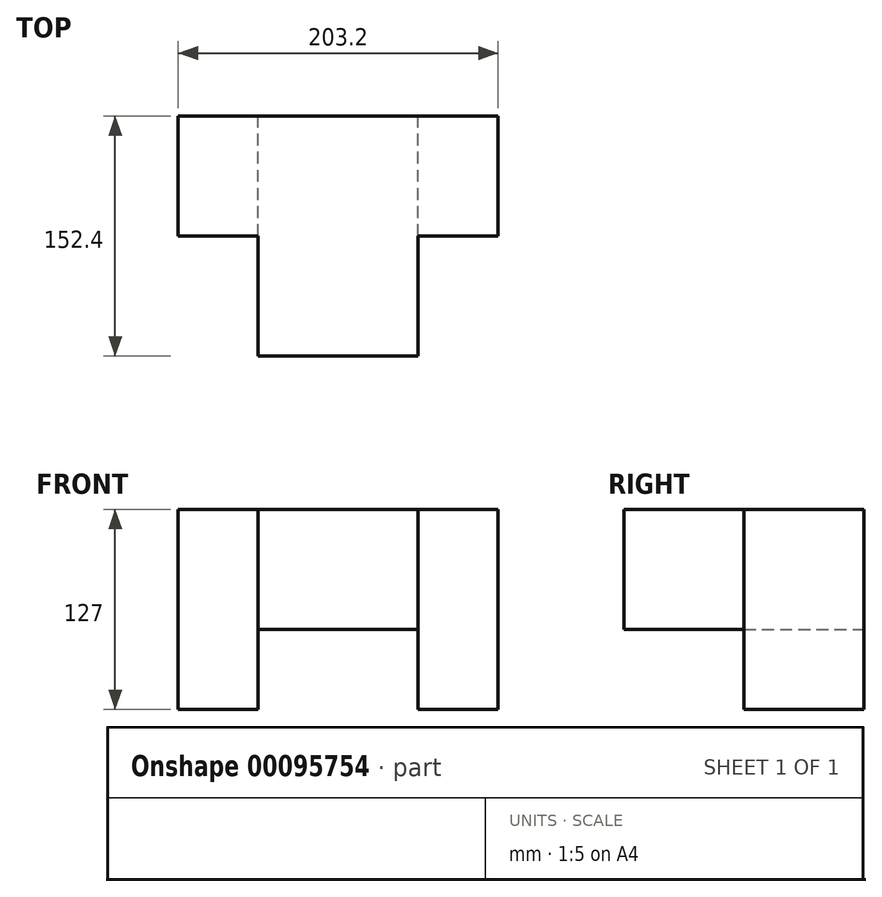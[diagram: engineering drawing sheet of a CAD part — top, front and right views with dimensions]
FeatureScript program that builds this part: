
annotation { "Feature Type Name" : "Feature", "Feature Type Description" : "" }
export const myFeature = defineFeature(function(context is Context, id is Id, definition is map)
    precondition{}
    {
        {
            var Q0;
            Q0=qCreatedBy(makeId("Front.planeOp"),FACE);
            var sketch = newSketch(context, id + "F0", { "sketchPlane" : qUnion([Q0])});
            skLineSegment(sketch, "E0.bottom", {"start": v(-54.53, 56.93) * mm, "end": v(47.07, 56.93) * mm});
            skLineSegment(sketch, "E0.top", {"start": v(-54.53, -19.27) * mm, "end": v(47.07, -19.27) * mm});
            skLineSegment(sketch, "E0.left", {"start": v(-54.53, 56.93) * mm, "end": v(-54.53, -19.27) * mm});
            skLineSegment(sketch, "E0.right", {"start": v(47.07, 56.93) * mm, "end": v(47.07, -19.27) * mm});
            skLineSegment(sketch, "E1.bottom", {"start": v(-54.53, 56.93) * mm, "end": v(-105.33, 56.93) * mm});
            skLineSegment(sketch, "E1.top", {"start": v(-54.53, -70.07) * mm, "end": v(-105.33, -70.07) * mm});
            skLineSegment(sketch, "E1.left", {"start": v(-54.53, 56.93) * mm, "end": v(-54.53, -70.07) * mm});
            skLineSegment(sketch, "E1.right", {"start": v(-105.33, 56.93) * mm, "end": v(-105.33, -70.07) * mm});
            skLineSegment(sketch, "E2.bottom", {"start": v(47.07, 56.93) * mm, "end": v(97.87, 56.93) * mm});
            skLineSegment(sketch, "E2.top", {"start": v(47.07, -70.07) * mm, "end": v(97.87, -70.07) * mm});
            skLineSegment(sketch, "E2.left", {"start": v(47.07, 56.93) * mm, "end": v(47.07, -70.07) * mm});
            skLineSegment(sketch, "E2.right", {"start": v(97.87, 56.93) * mm, "end": v(97.87, -70.07) * mm});
            skSolve(sketch);
        }
        {
            var Q0;
            Q0 = qSketchRegion(id + "F0", true);
            extrude(context, id + "F1", {"entities" : qUnion([Q0]), "depth" : 76.2 * mm});
        }
        {
            var Q0;
            Q0=makeQuery(id+"F1.opExtrude","CAP_FACE",FACE,{"disambiguationData":[OSD([sQuery(id+"F0.wireOp",EDGE,"E0.bottom"),sQuery(id+"F0.wireOp",EDGE,"E0.top"),sQuery(id+"F0.wireOp",EDGE,"E1.bottom"),sQuery(id+"F0.wireOp",EDGE,"E1.top"),sQuery(id+"F0.wireOp",EDGE,"E1.left"),sQuery(id+"F0.wireOp",EDGE,"E1.right"),sQuery(id+"F0.wireOp",EDGE,"E2.bottom"),sQuery(id+"F0.wireOp",EDGE,"E2.top"),sQuery(id+"F0.wireOp",EDGE,"E2.left"),sQuery(id+"F0.wireOp",EDGE,"E2.right")])],"isStart":false});
            var sketch = newSketch(context, id + "F2", { "sketchPlane" : qUnion([Q0])});
            skLineSegment(sketch, "E3", {"start": v(-54.53, -19.27) * mm, "end": v(-54.53, 56.93) * mm});
            skLineSegment(sketch, "E4", {"start": v(47.07, -19.27) * mm, "end": v(47.07, 56.93) * mm});
            skLineSegment(sketch, "E5", {"start": v(47.07, 56.93) * mm, "end": v(-54.53, 56.93) * mm});
            skLineSegment(sketch, "E6", {"start": v(-54.53, -19.27) * mm, "end": v(47.07, -19.27) * mm});
            skSolve(sketch);
        }
        {
            var Q0;
            Q0 = qSketchRegion(id + "F2", true);
            extrude(context, id + "F3", {"entities" : qUnion([Q0]), "operationType" : NewBodyOperationType.ADD, "depth" : 76.2 * mm});
        }
    });
